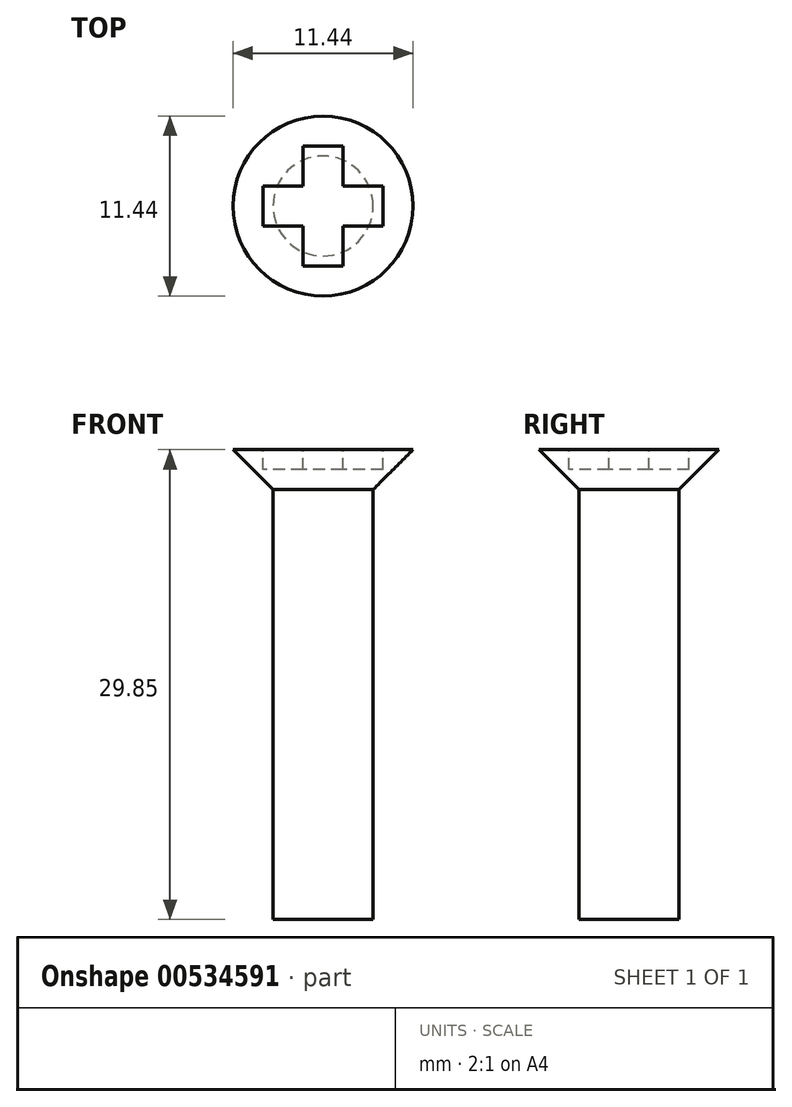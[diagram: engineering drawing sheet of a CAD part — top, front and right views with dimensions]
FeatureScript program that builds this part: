
annotation { "Feature Type Name" : "Feature", "Feature Type Description" : "" }
export const myFeature = defineFeature(function(context is Context, id is Id, definition is map)
    precondition{}
    {
        {
            var Q0;
            Q0=qCreatedBy(makeId("Top.planeOp"),FACE);
            var sketch = newSketch(context, id + "F0", { "sketchPlane" : qUnion([Q0])});
            skCircle(sketch, "E0", {"center": v(0, 0) * mm, "radius": 3.18 * mm});
            skSolve(sketch);
        }
        {
            var Q0;
            Q0=makeQuery(id+"F0.imprint","IMPRINT",FACE,{"disambiguationData":[TD([[makeQuery(id+"F0.imprint","IMPRINT",EDGE,{"derivedFrom":sQuery(id+"F0.wireOp",EDGE,"E0")}),1.0]])]});
            extrude(context, id + "F1", {"entities" : qUnion([Q0]), "depth" : 27.3 * mm, "offsetDistance" : 25.4 * mm});
        }
        {
            var Q0;
            Q0=makeQuery(id+"F1.opExtrude","CAP_FACE",FACE,{"disambiguationData":[OSD([sQuery(id+"F0.wireOp",EDGE,"E0")])],"isStart":false});
            extrude(context, id + "F2", {"entities" : qUnion([Q0]), "operationType" : NewBodyOperationType.ADD, "depth" : 2.54 * mm, "offsetDistance" : 25.4 * mm, "hasDraft" : true, "draftAngle" : 45 * degree});
        }
        {
            var Q0;
            Q0=makeQuery(id+"F2.opExtrude","CAP_FACE",FACE,{"disambiguationData":[OSD([sQuery(id+"F0.wireOp",EDGE,"E0")])],"isStart":false});
            var sketch = newSketch(context, id + "F3", { "sketchPlane" : qUnion([Q0])});
            skLineSegment(sketch, "E1.bottom", {"start": v(1.27, 3.8) * mm, "end": v(-1.27, 3.8) * mm});
            skLineSegment(sketch, "E1.top", {"start": v(1.27, -3.81) * mm, "end": v(-1.27, -3.81) * mm});
            skLineSegment(sketch, "E1.left", {"start": v(1.27, 3.8) * mm, "end": v(1.27, -3.8) * mm});
            skLineSegment(sketch, "E1.right", {"start": v(-1.27, 3.8) * mm, "end": v(-1.27, -3.81) * mm});
            skPoint(sketch, "E1.middle", {"position": v(0, 0) * mm});
            skLineSegment(sketch, "E2.bottom", {"start": v(3.81, 1.27) * mm, "end": v(-3.8, 1.27) * mm});
            skLineSegment(sketch, "E2.top", {"start": v(3.8, -1.27) * mm, "end": v(-3.81, -1.27) * mm});
            skLineSegment(sketch, "E2.left", {"start": v(3.81, 1.27) * mm, "end": v(3.81, -1.27) * mm});
            skLineSegment(sketch, "E2.right", {"start": v(-3.8, 1.27) * mm, "end": v(-3.8, -1.27) * mm});
            skSolve(sketch);
        }
        {
            var Q0;
            {var subQ0=sQuery(id+"F3.wireOp",EDGE,"E1.bottom");Q0=makeQuery(id+"F3.imprint","IMPRINT",FACE,{"disambiguationData":[TD([[makeQuery(id+"F3.imprint","IMPRINT",EDGE,{"derivedFrom":subQ0}),1.0]])]});}
            var Q1;
            {var subQ5=sQuery(id+"F3.wireOp",EDGE,"E2.right");Q1=makeQuery(id+"F3.imprint","IMPRINT",FACE,{"disambiguationData":[TD([[makeQuery(id+"F3.imprint","IMPRINT",EDGE,{"derivedFrom":subQ5}),1.0]])]});}
            var Q2;
            {var subQ0=sQuery(id+"F3.wireOp",EDGE,"E2.bottom");var subQ1=sQuery(id+"F3.wireOp",EDGE,"E1.left");var subQ2=makeQuery(id+"F3.imprint","INTERSECT",VERTEX,{"derivedFrom":[subQ1,subQ0]});Q2=makeQuery(id+"F3.imprint","IMPRINT",FACE,{"disambiguationData":[TD([[makeQuery(id+"F3.imprint","IMPRINT",EDGE,{"disambiguationData":[TD([[subQ2,-1.0]])],"derivedFrom":subQ1}),-1.0]])]});}
            var Q3;
            {var subQ5=sQuery(id+"F3.wireOp",EDGE,"E2.left");Q3=makeQuery(id+"F3.imprint","IMPRINT",FACE,{"disambiguationData":[TD([[makeQuery(id+"F3.imprint","IMPRINT",EDGE,{"derivedFrom":subQ5}),-1.0]])]});}
            var Q4;
            {var subQ0=sQuery(id+"F3.wireOp",EDGE,"E1.top");Q4=makeQuery(id+"F3.imprint","IMPRINT",FACE,{"disambiguationData":[TD([[makeQuery(id+"F3.imprint","IMPRINT",EDGE,{"derivedFrom":subQ0}),-1.0]])]});}
            extrude(context, id + "F4", {"entities" : qUnion([Q0, Q1, Q2, Q3, Q4]), "operationType" : NewBodyOperationType.REMOVE, "oppositeDirection" : true, "depth" : 1.27 * mm, "offsetDistance" : 25.4 * mm});
        }
    });
